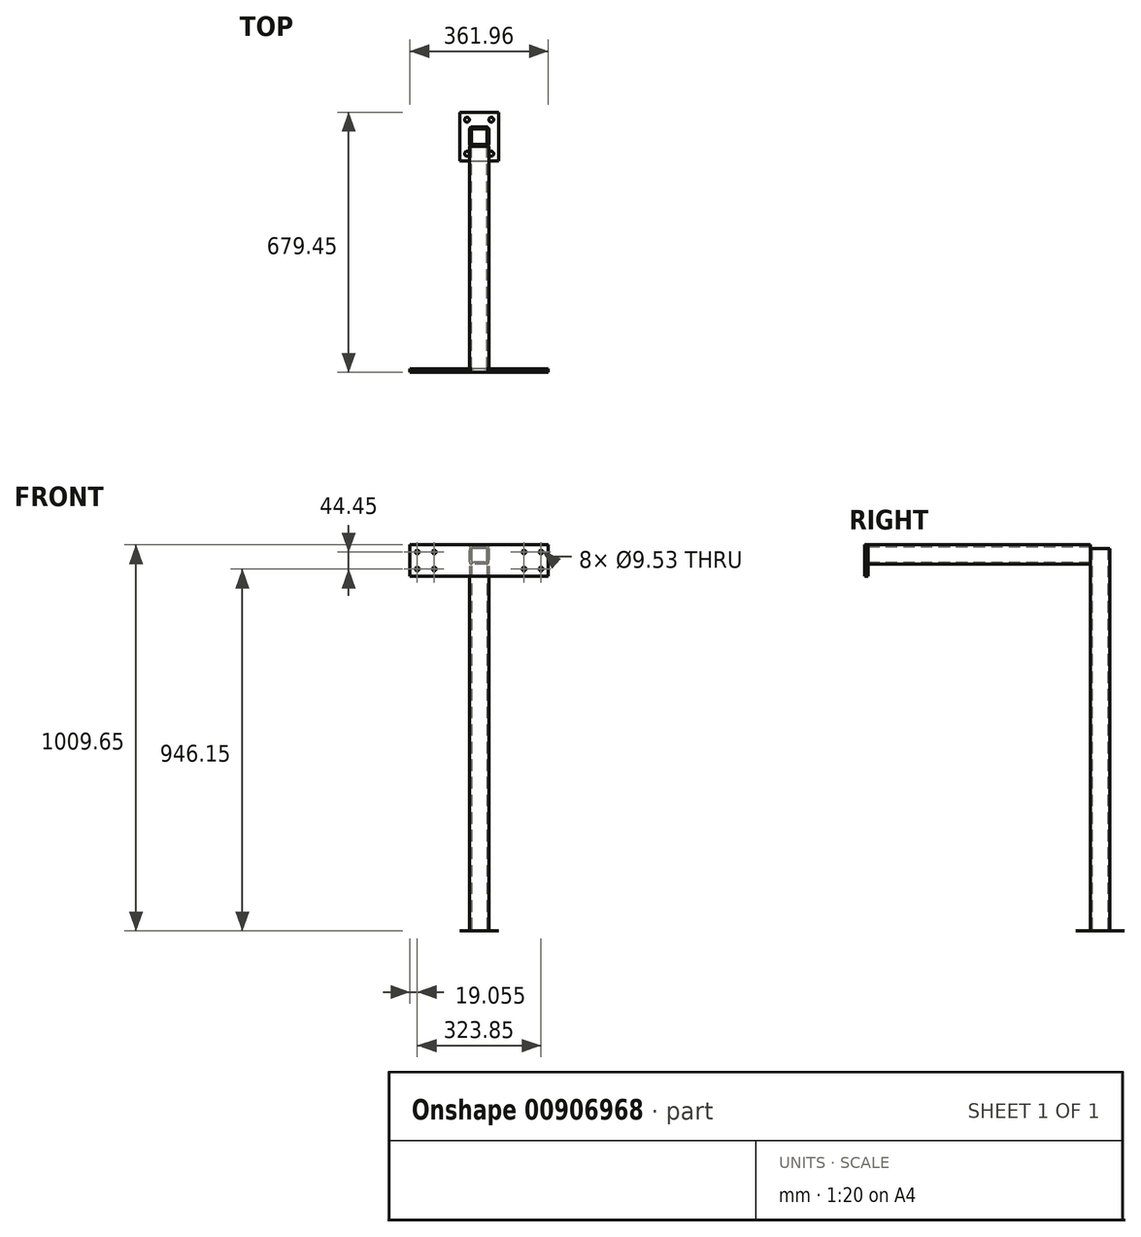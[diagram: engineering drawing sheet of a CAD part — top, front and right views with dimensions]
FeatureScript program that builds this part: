
annotation { "Feature Type Name" : "Feature", "Feature Type Description" : "" }
export const myFeature = defineFeature(function(context is Context, id is Id, definition is map)
    precondition{}
    {
        {
            var Q0;
            Q0=qCreatedBy(makeId("Top.planeOp"),FACE);
            var sketch = newSketch(context, id + "F0", { "sketchPlane" : qUnion([Q0])});
            skLineSegment(sketch, "E0.bottom", {"start": v(0, 0) * mm, "end": v(101.6, 0) * mm});
            skLineSegment(sketch, "E0.top", {"start": v(0, 127) * mm, "end": v(101.6, 127) * mm});
            skLineSegment(sketch, "E0.left", {"start": v(0, 0) * mm, "end": v(0, 127) * mm});
            skLineSegment(sketch, "E0.right", {"start": v(101.6, 0) * mm, "end": v(101.6, 127) * mm});
            skCircle(sketch, "E1", {"center": v(19.05, 107.95) * mm, "radius": 6.35 * mm});
            skCircle(sketch, "E2", {"center": v(82.55, 107.95) * mm, "radius": 6.35 * mm});
            skCircle(sketch, "E3", {"center": v(82.55, 19.05) * mm, "radius": 6.35 * mm});
            skCircle(sketch, "E4", {"center": v(19.05, 19.05) * mm, "radius": 6.35 * mm});
            skSolve(sketch);
        }
        {
            var Q0;
            Q0 = qSketchRegion(id + "F0", true);
            extrude(context, id + "F1", {"entities" : qUnion([Q0]), "depth" : 3 / 203.2 * mm, "offsetDistance" : 25.4 * mm});
        }
        {
            var Q0;
            Q0=qCreatedBy(makeId("Top.planeOp"),FACE);
            cPlane(context, id + "F2", {"entities" : qUnion([Q0]), "cplaneType" : CPlaneType.OFFSET, "offset" : 3 / 203.2 * mm, "width" : 152.4 * mm, "height" : 152.4 * mm});
        }
        {
            var Q0;
            Q0=qCreatedBy(id+"F2.planeOp",FACE);
            var sketch = newSketch(context, id + "F3", { "sketchPlane" : qUnion([Q0])});
            skLineSegment(sketch, "E5.bottom", {"start": v(69.85, 38.1) * mm, "end": v(31.75, 38.1) * mm});
            skLineSegment(sketch, "E5.top", {"start": v(69.85, 88.9) * mm, "end": v(31.75, 88.9) * mm});
            skLineSegment(sketch, "E5.left", {"start": v(76.2, 44.45) * mm, "end": v(76.2, 82.55) * mm});
            skLineSegment(sketch, "E5.right", {"start": v(25.4, 44.45) * mm, "end": v(25.4, 82.55) * mm});
            skLineSegment(sketch, "E6.bottom", {"start": v(65.09, 42.86) * mm, "end": v(36.51, 42.86) * mm});
            skLineSegment(sketch, "E6.top", {"start": v(65.09, 84.14) * mm, "end": v(36.51, 84.14) * mm});
            skLineSegment(sketch, "E6.left", {"start": v(71.44, 49.21) * mm, "end": v(71.44, 77.79) * mm});
            skLineSegment(sketch, "E6.right", {"start": v(30.16, 49.21) * mm, "end": v(30.16, 77.79) * mm});
            skPoint(sketch, "E7.visualSharp", {"position": v(25.4, 88.9) * mm});
            skArc(sketch, "E7.filletArc", {"start": v(31.75, 88.9) * mm, "mid": v(27.26, 87.04) * mm, "end": v(25.4, 82.55) * mm});
            skPoint(sketch, "E8.visualSharp", {"position": v(76.2, 88.9) * mm});
            skArc(sketch, "E8.filletArc", {"start": v(76.2, 82.55) * mm, "mid": v(74.34, 87.04) * mm, "end": v(69.85, 88.9) * mm});
            skPoint(sketch, "E9.visualSharp", {"position": v(76.2, 38.1) * mm});
            skArc(sketch, "E9.filletArc", {"start": v(69.85, 38.1) * mm, "mid": v(74.34, 39.96) * mm, "end": v(76.2, 44.45) * mm});
            skPoint(sketch, "E10.visualSharp", {"position": v(25.4, 38.1) * mm});
            skArc(sketch, "E10.filletArc", {"start": v(25.4, 44.45) * mm, "mid": v(27.26, 39.96) * mm, "end": v(31.75, 38.1) * mm});
            skPoint(sketch, "E11.visualSharp", {"position": v(30.16, 42.86) * mm});
            skArc(sketch, "E11.filletArc", {"start": v(30.16, 49.21) * mm, "mid": v(32.02, 44.72) * mm, "end": v(36.51, 42.86) * mm});
            skPoint(sketch, "E12.visualSharp", {"position": v(30.16, 84.14) * mm});
            skArc(sketch, "E12.filletArc", {"start": v(36.51, 84.14) * mm, "mid": v(32.02, 82.28) * mm, "end": v(30.16, 77.79) * mm});
            skPoint(sketch, "E13.visualSharp", {"position": v(71.44, 84.14) * mm});
            skArc(sketch, "E13.filletArc", {"start": v(71.44, 77.79) * mm, "mid": v(69.58, 82.28) * mm, "end": v(65.09, 84.14) * mm});
            skPoint(sketch, "E14.visualSharp", {"position": v(71.44, 42.86) * mm});
            skArc(sketch, "E14.filletArc", {"start": v(65.09, 42.86) * mm, "mid": v(69.58, 44.72) * mm, "end": v(71.44, 49.21) * mm});
            skSolve(sketch);
        }
        {
            var Q0;
            Q0 = qSketchRegion(id + "F3", true);
            extrude(context, id + "F4", {"entities" : qUnion([Q0]), "operationType" : NewBodyOperationType.ADD, "depth" : 1000.12 * mm, "offsetDistance" : 25.4 * mm});
        }
        {
            var Q0;
            Q0=makeQuery(id+"F4.opExtrude","SWEPT_FACE",FACE,{"disambiguationData":[OSD([sQuery(id+"F3.wireOp",EDGE,"E5.bottom")])]});
            var sketch = newSketch(context, id + "F5", { "sketchPlane" : qUnion([Q0])});
            skLineSegment(sketch, "E15.bottom", {"start": v(69.85, 958.85) * mm, "end": v(31.75, 958.85) * mm});
            skLineSegment(sketch, "E15.top", {"start": v(69.85, 1009.65) * mm, "end": v(31.75, 1009.65) * mm});
            skLineSegment(sketch, "E15.left", {"start": v(76.2, 965.2) * mm, "end": v(76.2, 1003.3) * mm});
            skLineSegment(sketch, "E15.right", {"start": v(25.4, 965.2) * mm, "end": v(25.4, 1003.3) * mm});
            skLineSegment(sketch, "E16.bottom", {"start": v(65.09, 963.61) * mm, "end": v(36.51, 963.61) * mm});
            skLineSegment(sketch, "E16.top", {"start": v(65.09, 1004.89) * mm, "end": v(36.51, 1004.89) * mm});
            skLineSegment(sketch, "E16.left", {"start": v(71.44, 969.96) * mm, "end": v(71.44, 998.54) * mm});
            skLineSegment(sketch, "E16.right", {"start": v(30.16, 969.96) * mm, "end": v(30.16, 998.54) * mm});
            skPoint(sketch, "E17.visualSharp", {"position": v(25.4, 1009.65) * mm});
            skArc(sketch, "E17.filletArc", {"start": v(31.75, 1009.65) * mm, "mid": v(27.26, 1007.8) * mm, "end": v(25.4, 1003.3) * mm});
            skPoint(sketch, "E18.visualSharp", {"position": v(30.16, 1004.89) * mm});
            skArc(sketch, "E18.filletArc", {"start": v(36.51, 1004.89) * mm, "mid": v(32.02, 1003.03) * mm, "end": v(30.16, 998.54) * mm});
            skPoint(sketch, "E19.visualSharp", {"position": v(71.44, 1004.89) * mm});
            skArc(sketch, "E19.filletArc", {"start": v(71.44, 998.54) * mm, "mid": v(69.58, 1003.03) * mm, "end": v(65.09, 1004.89) * mm});
            skPoint(sketch, "E20.visualSharp", {"position": v(76.2, 1009.65) * mm});
            skArc(sketch, "E20.filletArc", {"start": v(76.2, 1003.3) * mm, "mid": v(74.34, 1007.8) * mm, "end": v(69.85, 1009.65) * mm});
            skPoint(sketch, "E21.visualSharp", {"position": v(71.44, 963.61) * mm});
            skArc(sketch, "E21.filletArc", {"start": v(65.09, 963.61) * mm, "mid": v(69.58, 965.47) * mm, "end": v(71.44, 969.96) * mm});
            skPoint(sketch, "E22.visualSharp", {"position": v(76.2, 958.85) * mm});
            skArc(sketch, "E22.filletArc", {"start": v(69.85, 958.85) * mm, "mid": v(74.34, 960.7) * mm, "end": v(76.2, 965.2) * mm});
            skPoint(sketch, "E23.visualSharp", {"position": v(30.16, 963.61) * mm});
            skArc(sketch, "E23.filletArc", {"start": v(30.16, 969.96) * mm, "mid": v(32.02, 965.47) * mm, "end": v(36.51, 963.61) * mm});
            skPoint(sketch, "E24.visualSharp", {"position": v(25.4, 958.85) * mm});
            skArc(sketch, "E24.filletArc", {"start": v(25.4, 965.2) * mm, "mid": v(27.26, 960.7) * mm, "end": v(31.75, 958.85) * mm});
            skSolve(sketch);
        }
        {
            var Q0;
            Q0 = qSketchRegion(id + "F5", true);
            extrude(context, id + "F6", {"entities" : qUnion([Q0]), "operationType" : NewBodyOperationType.ADD, "depth" : 581.02 * mm, "offsetDistance" : 25.4 * mm});
        }
        {
            var Q0;
            Q0=makeQuery(id+"F6.opExtrude","CAP_FACE",FACE,{"disambiguationData":[OSD([sQuery(id+"F5.wireOp",EDGE,"E15.bottom"),sQuery(id+"F5.wireOp",EDGE,"E15.top"),sQuery(id+"F5.wireOp",EDGE,"E15.left"),sQuery(id+"F5.wireOp",EDGE,"E15.right"),sQuery(id+"F5.wireOp",EDGE,"E16.bottom"),sQuery(id+"F5.wireOp",EDGE,"E16.top"),sQuery(id+"F5.wireOp",EDGE,"E16.left"),sQuery(id+"F5.wireOp",EDGE,"E16.right"),sQuery(id+"F5.wireOp",EDGE,"E17.filletArc"),sQuery(id+"F5.wireOp",EDGE,"E18.filletArc"),sQuery(id+"F5.wireOp",EDGE,"E19.filletArc"),sQuery(id+"F5.wireOp",EDGE,"E20.filletArc"),sQuery(id+"F5.wireOp",EDGE,"E21.filletArc"),sQuery(id+"F5.wireOp",EDGE,"E22.filletArc"),sQuery(id+"F5.wireOp",EDGE,"E23.filletArc"),sQuery(id+"F5.wireOp",EDGE,"E24.filletArc")])],"isStart":false});
            var sketch = newSketch(context, id + "F7", { "sketchPlane" : qUnion([Q0])});
            skLineSegment(sketch, "E25.bottom", {"start": v(231.77, 927.1) * mm, "end": v(-130.18, 927.1) * mm});
            skLineSegment(sketch, "E25.top", {"start": v(231.77, 1009.65) * mm, "end": v(-130.18, 1009.65) * mm});
            skLineSegment(sketch, "E25.left", {"start": v(231.77, 927.1) * mm, "end": v(231.77, 1009.65) * mm});
            skLineSegment(sketch, "E25.right", {"start": v(-130.18, 927.1) * mm, "end": v(-130.18, 1009.65) * mm});
            skCircle(sketch, "E26", {"center": v(168.27, 990.6) * mm, "radius": 4.76 * mm});
            skCircle(sketch, "E27", {"center": v(212.72, 990.6) * mm, "radius": 4.76 * mm});
            skCircle(sketch, "E28", {"center": v(168.27, 946.15) * mm, "radius": 4.76 * mm});
            skCircle(sketch, "E29", {"center": v(212.72, 946.15) * mm, "radius": 4.76 * mm});
            skLineSegment(sketch, "E30", {"start": v(50.8, 1004.89) * mm, "end": v(50.8, 963.61) * mm});
            skCircle(sketch, "E31.MirrorC", {"center": v(-111.13, 946.15) * mm, "radius": 4.76 * mm});
            skCircle(sketch, "E32.MirrorC", {"center": v(-66.68, 946.15) * mm, "radius": 4.76 * mm});
            skCircle(sketch, "E33.MirrorC", {"center": v(-111.13, 990.6) * mm, "radius": 4.76 * mm});
            skCircle(sketch, "E34.MirrorC", {"center": v(-66.68, 990.6) * mm, "radius": 4.76 * mm});
            skSolve(sketch);
        }
        {
            var Q0;
            Q0 = qSketchRegion(id + "F7", true);
            extrude(context, id + "F8", {"entities" : qUnion([Q0]), "operationType" : NewBodyOperationType.ADD, "depth" : 9.52 * mm, "offsetDistance" : 25.4 * mm});
        }
    });
